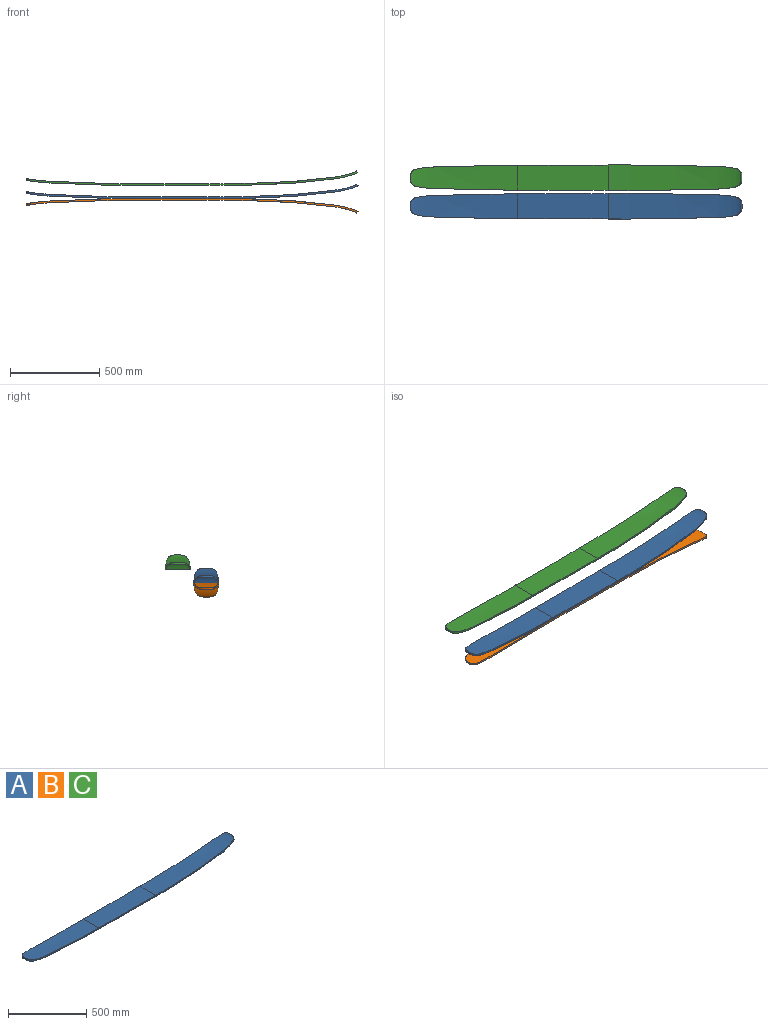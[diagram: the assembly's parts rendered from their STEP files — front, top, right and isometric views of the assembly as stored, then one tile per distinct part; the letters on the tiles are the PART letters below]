
ASSEMBLY  parts=3 mates=1
PART A: 30 faces, bbox 1860x143.7x81.2 mm
  f0: bspline ~104.52x20.48mm, area 1049.3mm2, adj f1,f23,f24,f27
  f1: bspline ~38.89x32.13mm, area 534.1mm2, adj f0,f2,f24,f27
  f2: plane 17.37x9.66mm, normal (-0.97,0,0.26), area 173.7mm2, adj f1,f3,f24,f27
  f3: bspline ~38.89x32.13mm, area 534.1mm2, adj f2,f4,f24,f27
  f4: bspline ~104.52x20.48mm, area 1049.3mm2, adj f3,f5,f24,f27
  f5: bspline ~319.07x22.27mm, area 3190mm2, adj f4,f6,f24,f27
  f6: bspline ~146.66x11.12mm, area 1466mm2, adj f5,f7,f24,f27
  f7: cylinder r=7500mm len=10mm, axis (0,0,1), area 74.8mm2, adj f6,f8,f25,f28
  f8: extruded ~476.63x10mm, area 4766.4mm2, adj f7,f9,f25,f28
  f9: cylinder r=7500mm len=25.89mm, axis (0,0,1), area 258.9mm2, adj f8,f10,f25,f28
  f10: bspline ~123.41x11.15mm, area 1233.3mm2, adj f9,f11,f26,f29
  f11: bspline ~493.41x44.89mm, area 4941.8mm2, adj f10,f12,f26,f29
  f12: bspline ~104.11x32.23mm, area 1052mm2, adj f11,f13,f26,f29
  f13: bspline ~38.93x34.01mm, area 547.3mm2, adj f12,f14,f26,f29
  f14: plane 24.13x8.19mm, normal (0.82,0,0.57), area 241.3mm2, adj f13,f15,f26,f29
  f15: bspline ~38.93x34.01mm, area 547.3mm2, adj f14,f16,f26,f29
  f16: bspline ~104.11x32.23mm, area 1052mm2, adj f15,f17,f26,f29
  f17: bspline ~493.41x44.89mm, area 4941.8mm2, adj f16,f18,f26,f29
  f18: bspline ~123.41x11.15mm, area 1233.3mm2, adj f17,f19,f26,f29
  f19: cylinder r=7500mm len=25.89mm, axis (0,0,1), area 258.9mm2, adj f18,f20,f25,f28
  f20: extruded ~476.63x10mm, area 4766.4mm2, adj f19,f21,f25,f28
  f21: cylinder r=7500mm len=10mm, axis (0,0,1), area 74.8mm2, adj f20,f22,f25,f28
  f22: bspline ~146.66x11.12mm, area 1466mm2, adj f21,f23,f24,f27
  f23: bspline ~319.07x22.27mm, area 3190mm2, adj f0,f22,f24,f27
  f24: extruded ~597.41x138.37mm, area 74658.6mm2, adj f0,f1,f2,f3,f4,f5,f6,f22
  f25: plane 510x142.93mm, normal (0,0,1), area 71060.4mm2, adj f7,f8,f9,f19,f20,f21,f24,f26
  f26: extruded ~744.26x143mm, area 98969.2mm2, adj f10,f11,f12,f13,f14,f15,f16,f17
  f27: extruded ~600x138.37mm, area 74618.8mm2, adj f0,f1,f2,f3,f4,f5,f6,f22
  f28: plane 510x142.93mm, normal (0,0,-1), area 71060.4mm2, adj f7,f8,f9,f19,f20,f21,f27,f29
  f29: extruded ~750x143mm, area 99467.3mm2, adj f10,f11,f12,f13,f14,f15,f16,f17
PART B: same geometry as A
PART C: same geometry as A
PLACE A t=(-195.65,-385.39,164.84)mm
PLACE B rot(axis=(1,0,0),180deg) t=(-195.65,-385.39,-15.16)mm
PLACE C t=(-196.02,-225.86,238.45)mm
MATE fastened B.f28 <-> A.f28  axis (0,0,1) through (-319.24,-385.39,74.84)mm
